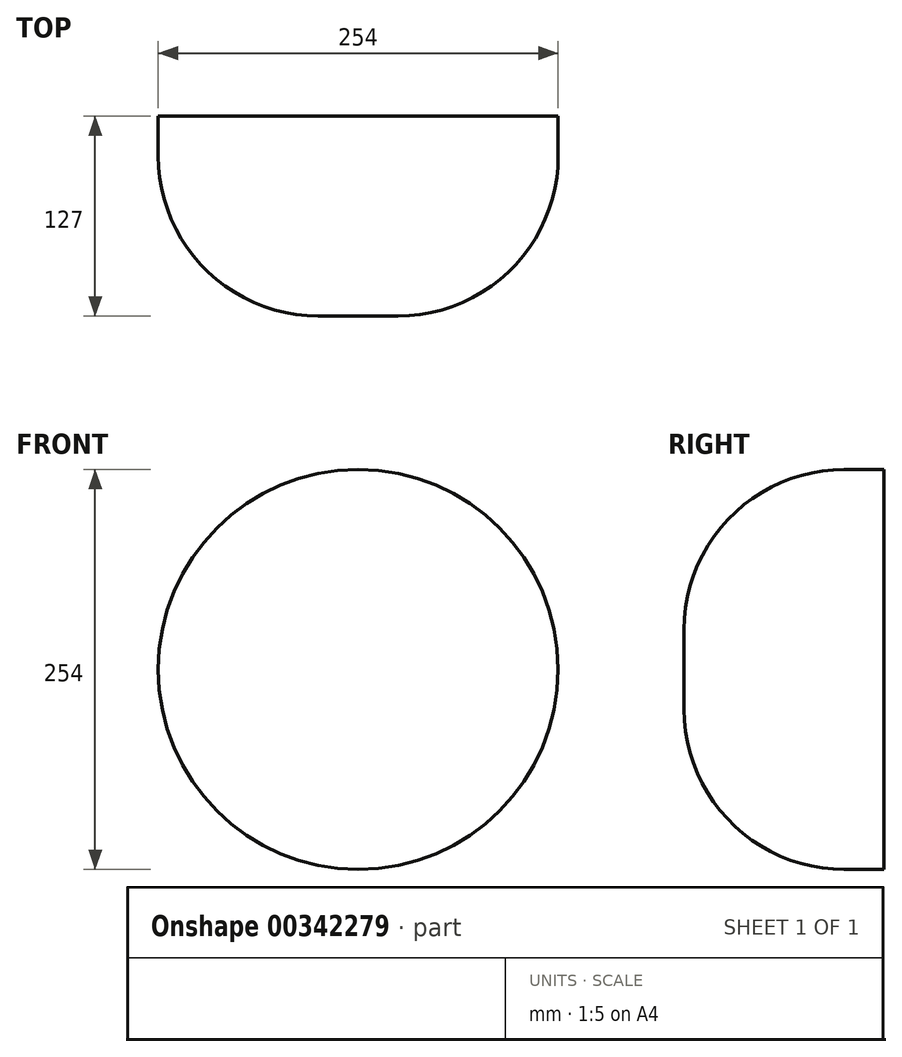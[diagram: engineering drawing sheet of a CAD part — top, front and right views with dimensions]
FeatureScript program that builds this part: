
annotation { "Feature Type Name" : "Feature", "Feature Type Description" : "" }
export const myFeature = defineFeature(function(context is Context, id is Id, definition is map)
    precondition{}
    {
        {
            var Q0;
            Q0=qCreatedBy(makeId("Front.planeOp"),FACE);
            var sketch = newSketch(context, id + "F0", { "sketchPlane" : qUnion([Q0])});
            skCircle(sketch, "E0", {"center": v(0, 0) * mm, "radius": 127 * mm});
            skSolve(sketch);
        }
        {
            var Q0;
            Q0=makeQuery(id+"F0.imprint","IMPRINT",FACE,{"disambiguationData":[TD([[makeQuery(id+"F0.imprint","IMPRINT",EDGE,{"derivedFrom":sQuery(id+"F0.wireOp",EDGE,"E0")}),1.0]])]});
            extrude(context, id + "F1", {"entities" : qUnion([Q0]), "depth" : 127 * mm});
        }
        {
            var Q0;
            Q0=makeQuery(id+"F1.opExtrude","CAP_EDGE",EDGE,{"disambiguationData":[OSD([sQuery(id+"F0.wireOp",EDGE,"E0")])],"isStart":false});
            fillet(context, id + "F2", {"entities" : qUnion([Q0]), "radius" : 101.6 * mm, "tangentPropagation" : true, "allowEdgeOverflow" : false});
        }
        {
            var Q0;
            Q0=qCreatedBy(makeId("Right.planeOp"),FACE);
            var sketch = newSketch(context, id + "F3", { "sketchPlane" : qUnion([Q0])});
            skFitSpline(sketch, "E1", {"points": [v(-116.02, 90.14) * mm, v(-143.44, 47.24) * mm, v(-148.27, 0) * mm, v(-145.05, 0) * mm, v(-133.12, 49.18) * mm, v(-102.8, 94.33) * mm, v(-101.84, 107.23) * mm, v(-116.02, 90.14) * mm]});
            skSolve(sketch);
        }
        {
            var Q0;
            Q0=sQuery(id+"F3.wireOp",EDGE,"E1");
            extrude(context, id + "F4", {"bodyType" : ToolBodyType.SURFACE, "surfaceEntities" : qUnion([Q0]), "depth" : 25.4 * mm});
        }
    });
